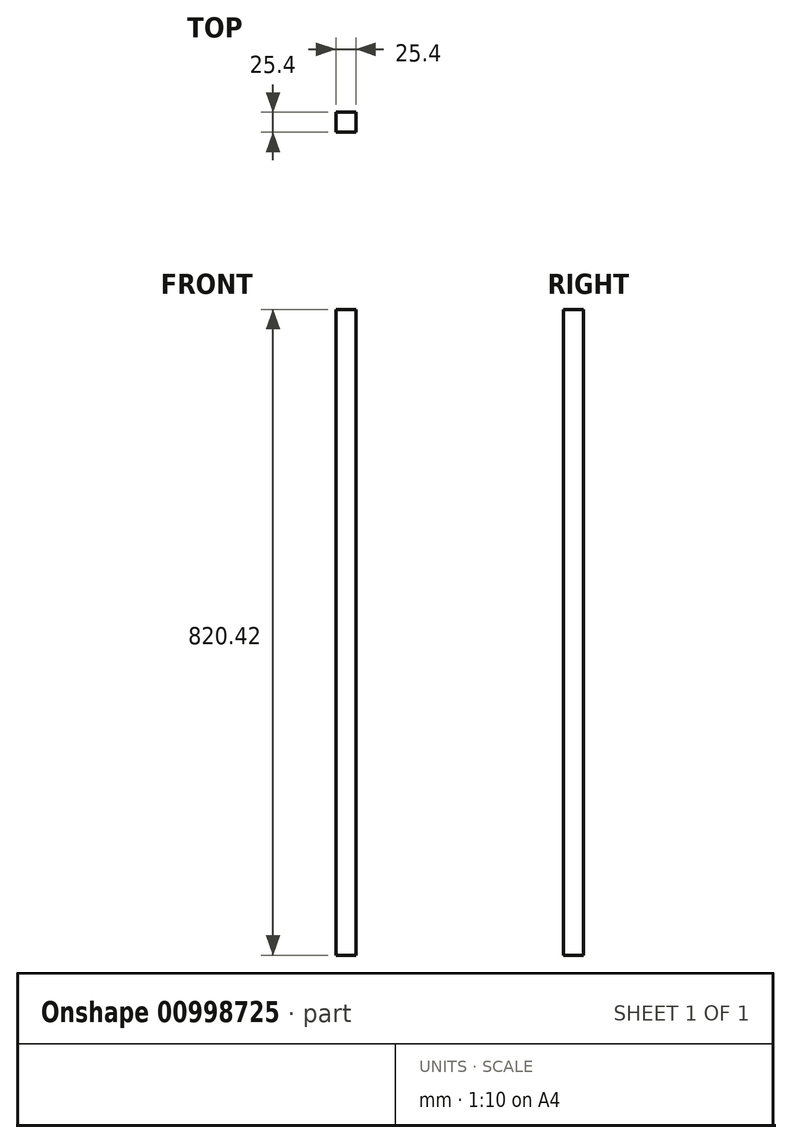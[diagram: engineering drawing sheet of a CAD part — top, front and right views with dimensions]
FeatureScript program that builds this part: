
annotation { "Feature Type Name" : "Feature", "Feature Type Description" : "" }
export const myFeature = defineFeature(function(context is Context, id is Id, definition is map)
    precondition{}
    {
        {
            var Q0;
            Q0=qCreatedBy(makeId("Front.planeOp"),FACE);
            var sketch = newSketch(context, id + "F0", { "sketchPlane" : qUnion([Q0])});
            skLineSegment(sketch, "E0.bottom", {"start": v(-60.86, 746.4) * mm, "end": v(-35.46, 746.4) * mm});
            skLineSegment(sketch, "E0.top", {"start": v(-60.86, -74.03) * mm, "end": v(-35.46, -74.03) * mm});
            skLineSegment(sketch, "E0.left", {"start": v(-60.86, 746.4) * mm, "end": v(-60.86, -74.03) * mm});
            skLineSegment(sketch, "E0.right", {"start": v(-35.46, 746.4) * mm, "end": v(-35.46, -74.03) * mm});
            skSolve(sketch);
        }
        {
            var Q0;
            Q0=makeQuery(id+"F0.imprint","IMPRINT",FACE,{"disambiguationData":[TD([[makeQuery(id+"F0.imprint","IMPRINT",EDGE,{"derivedFrom":sQuery(id+"F0.wireOp",EDGE,"E0.bottom")}),-1.0]])]});
            extrude(context, id + "F1", {"entities" : qUnion([Q0]), "depth" : 25.4 * mm, "offsetDistance" : 25.4 * mm});
        }
    });
